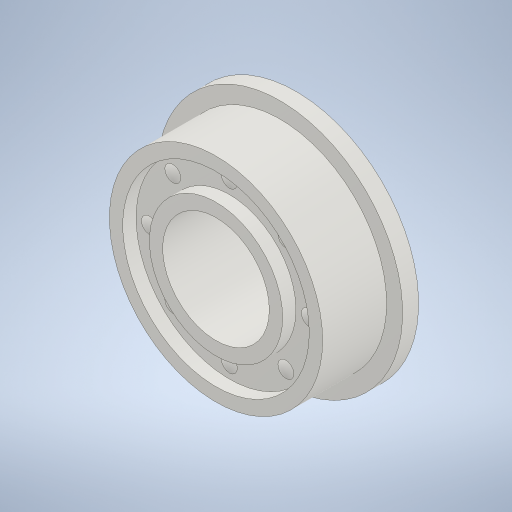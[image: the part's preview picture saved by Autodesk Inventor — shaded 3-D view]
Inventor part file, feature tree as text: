
AUTODESK INVENTOR PART (.ipt)
format: ipt  version: 2023 (Build 270158030, 158C)  size: 336,896 bytes
history: native  units: mm
features: sketch x7, other x4, extrude x4, revolve x1, pattern_circular x1
ambient origin geometry x8: Origin, YZ Plane, XZ Plane, XY Plane, X Axis, Y Axis, Z Axis, Center Point
bodies: Body1 (feature_tree)
feature tree (17):
  other  "ソリッド1"
  extrude  "押し出し1"  Depth=4.0mm
  sketch  "スケッチ2"
  other  "作業平面1"
  other  "作業平面2"
  other  "作業平面3"
  revolve  "回転1"
  pattern_circular  "円形状パターン1"  [2 undecoded]
  extrude  "押し出し2"  Depth=8.0mm
  extrude  "押し出し3"  Depth=7.0mm
  extrude  "押し出し4"  Depth=2.4mm TaperAngle=0.0deg
  sketch  "スケッチ7"
  sketch  "スケッチ1"
  sketch  "スケッチ3"
  sketch  "スケッチ4"
  sketch  "スケッチ5"
  sketch  "スケッチ6"
note: 2 required parameter values undecoded (feature->parameter linkage not recoverable at this tier; creation-order binding heuristic only, values carry confidence <= 0.55)
